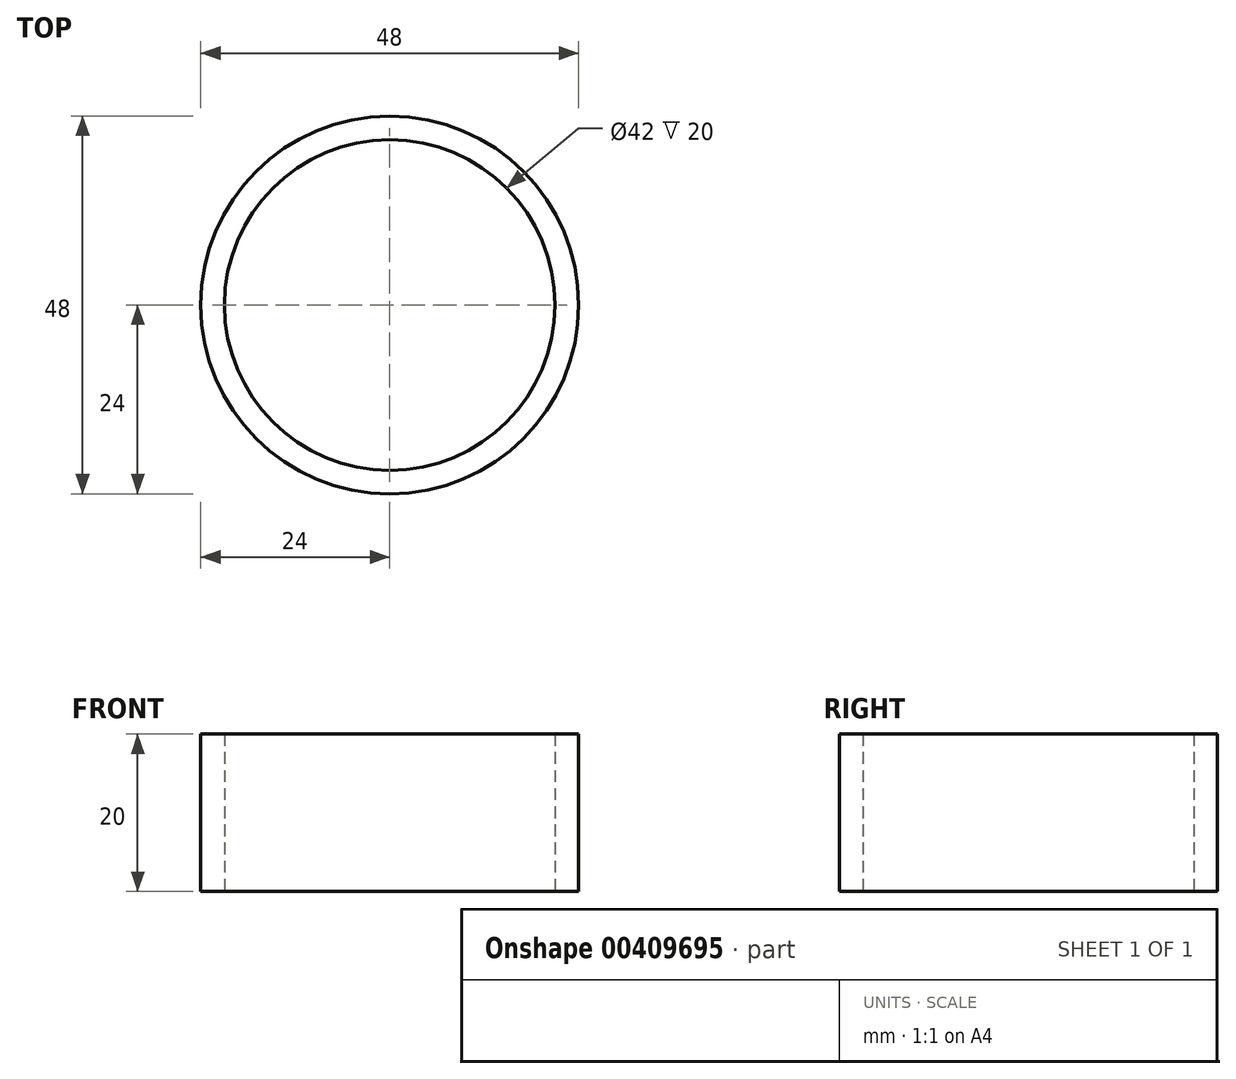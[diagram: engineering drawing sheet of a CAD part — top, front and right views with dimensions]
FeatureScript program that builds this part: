
annotation { "Feature Type Name" : "Feature", "Feature Type Description" : "" }
export const myFeature = defineFeature(function(context is Context, id is Id, definition is map)
    precondition{}
    {
        {
            var Q0;
            Q0=qCreatedBy(makeId("Top.planeOp"),FACE);
            var sketch = newSketch(context, id + "F0", { "sketchPlane" : qUnion([Q0])});
            skCircle(sketch, "E0", {"center": v(0, 0) * mm, "radius": 24 * mm});
            skCircle(sketch, "E1", {"center": v(0, 0) * mm, "radius": 21 * mm});
            skLineSegment(sketch, "E2", {"start": v(21, 0) * mm, "end": v(24, 0) * mm, "construction": true});
            skSolve(sketch);
        }
        {
            var Q0;
            Q0 = qSketchRegion(id + "F0", true);
            extrude(context, id + "F1", {"entities" : qUnion([Q0]), "depth" : 20 * mm});
        }
    });
